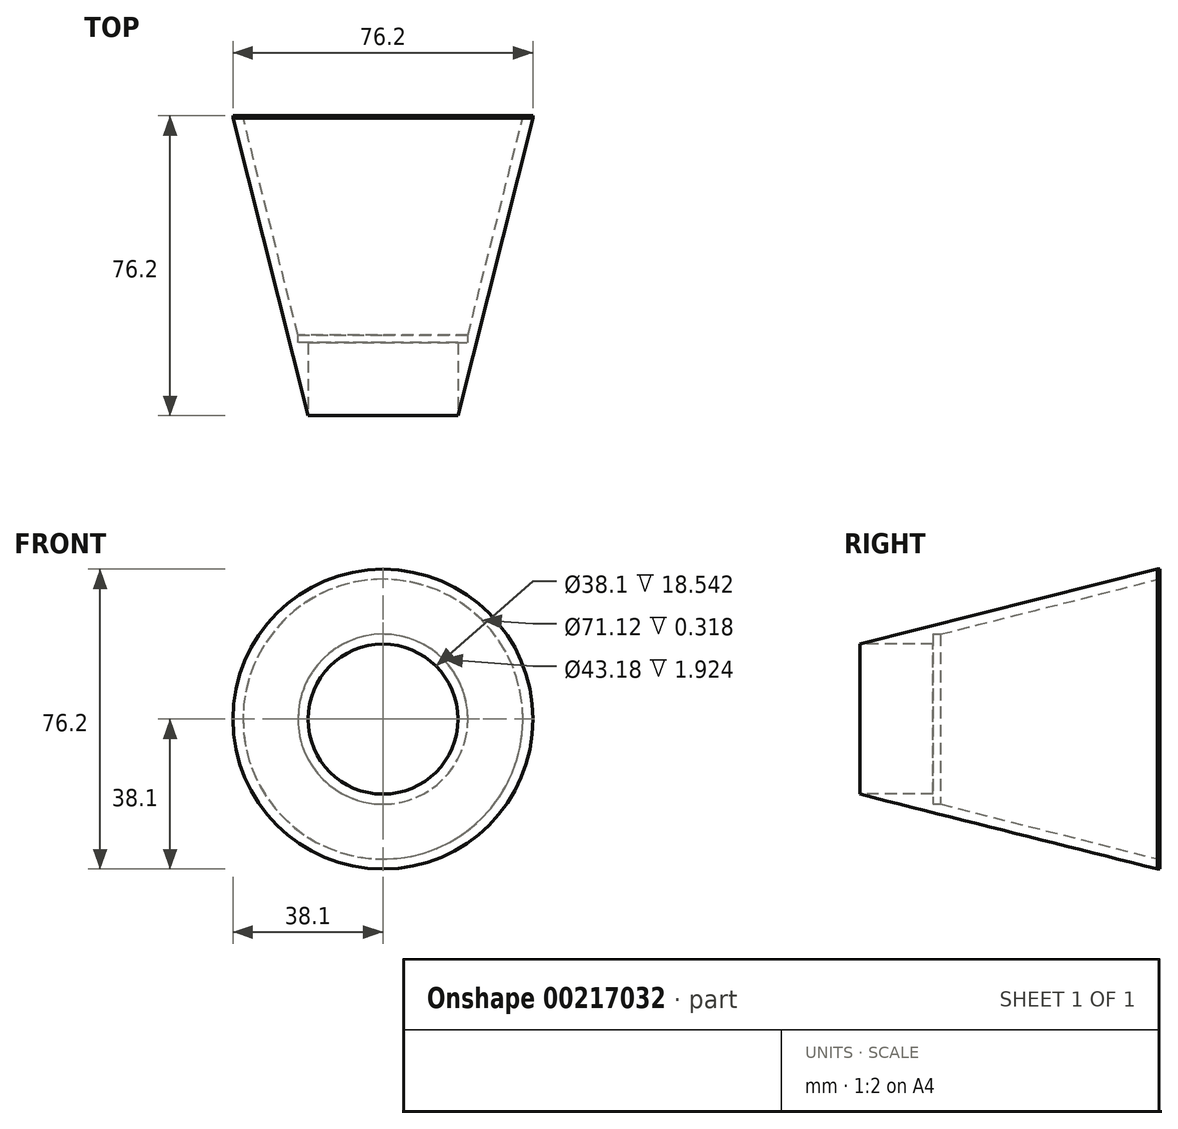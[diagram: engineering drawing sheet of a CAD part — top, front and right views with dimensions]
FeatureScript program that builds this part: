
annotation { "Feature Type Name" : "Feature", "Feature Type Description" : "" }
export const myFeature = defineFeature(function(context is Context, id is Id, definition is map)
    precondition{}
    {
        {
            var Q0;
            Q0=qCreatedBy(makeId("Front.planeOp"),FACE);
            var sketch = newSketch(context, id + "F0", { "sketchPlane" : qUnion([Q0])});
            skCircle(sketch, "E0", {"center": v(0, 0) * mm, "radius": 19.05 * mm});
            skCircle(sketch, "E1", {"center": v(0, 0) * mm, "radius": 38.1 * mm});
            skSolve(sketch);
        }
        {
            var Q0;
            Q0 = qSketchRegion(id + "F0", true);
            extrude(context, id + "F1", {"entities" : qUnion([Q0]), "oppositeDirection" : true, "depth" : 76.2 * mm});
        }
        {
            var Q0;
            Q0=qCreatedBy(makeId("Right.planeOp"),FACE);
            var sketch = newSketch(context, id + "F2", { "sketchPlane" : qUnion([Q0])});
            skLineSegment(sketch, "E2", {"start": v(0, 0) * mm, "end": v(0, 19.05) * mm});
            skLineSegment(sketch, "E3", {"start": v(0, 19.05) * mm, "end": v(89.66, 41.65) * mm});
            skLineSegment(sketch, "E4", {"start": v(89.66, 41.65) * mm, "end": v(-15.24, 41.65) * mm});
            skLineSegment(sketch, "E5", {"start": v(-15.24, 41.65) * mm, "end": v(0, 19.05) * mm});
            skSolve(sketch);
        }
        {
            var Q0;
            Q0 = qSketchRegion(id + "F2", true);
            var Q1;
            Q1=makeQuery(id+"F1.opExtrude","CAP_EDGE",EDGE,{"disambiguationData":[OSD([sQuery(id+"F0.wireOp",EDGE,"E1")])],"isStart":false});
            revolve(context, id + "F3", {"operationType" : NewBodyOperationType.REMOVE, "entities" : qUnion([Q0]), "axis" : qUnion([Q1]), "revolveType" : RevolveType.FULL, "oppositeDirection" : true});
        }
        {
            var Q0;
            Q0=makeQuery(id+"F1.opExtrude","CAP_FACE",FACE,{"disambiguationData":[OSD([sQuery(id+"F0.wireOp",EDGE,"E0"),sQuery(id+"F0.wireOp",EDGE,"E1")])],"isStart":false});
            shell(context, id + "F4", {"entities" : qUnion([Q0]), "thickness" : 2.54 * mm});
        }
        {
            var Q0;
            Q0=makeQuery(id+"F4.opShell","OFFSET_FACE",FACE,{"disambiguationData":[OSD([sQuery(id+"F0.wireOp",EDGE,"E0"),sQuery(id+"F0.wireOp",EDGE,"E1")])]});
            extrude(context, id + "F5", {"entities" : qUnion([Q0]), "operationType" : NewBodyOperationType.REMOVE, "oppositeDirection" : true, "depth" : 57.66 * mm});
        }
    });
